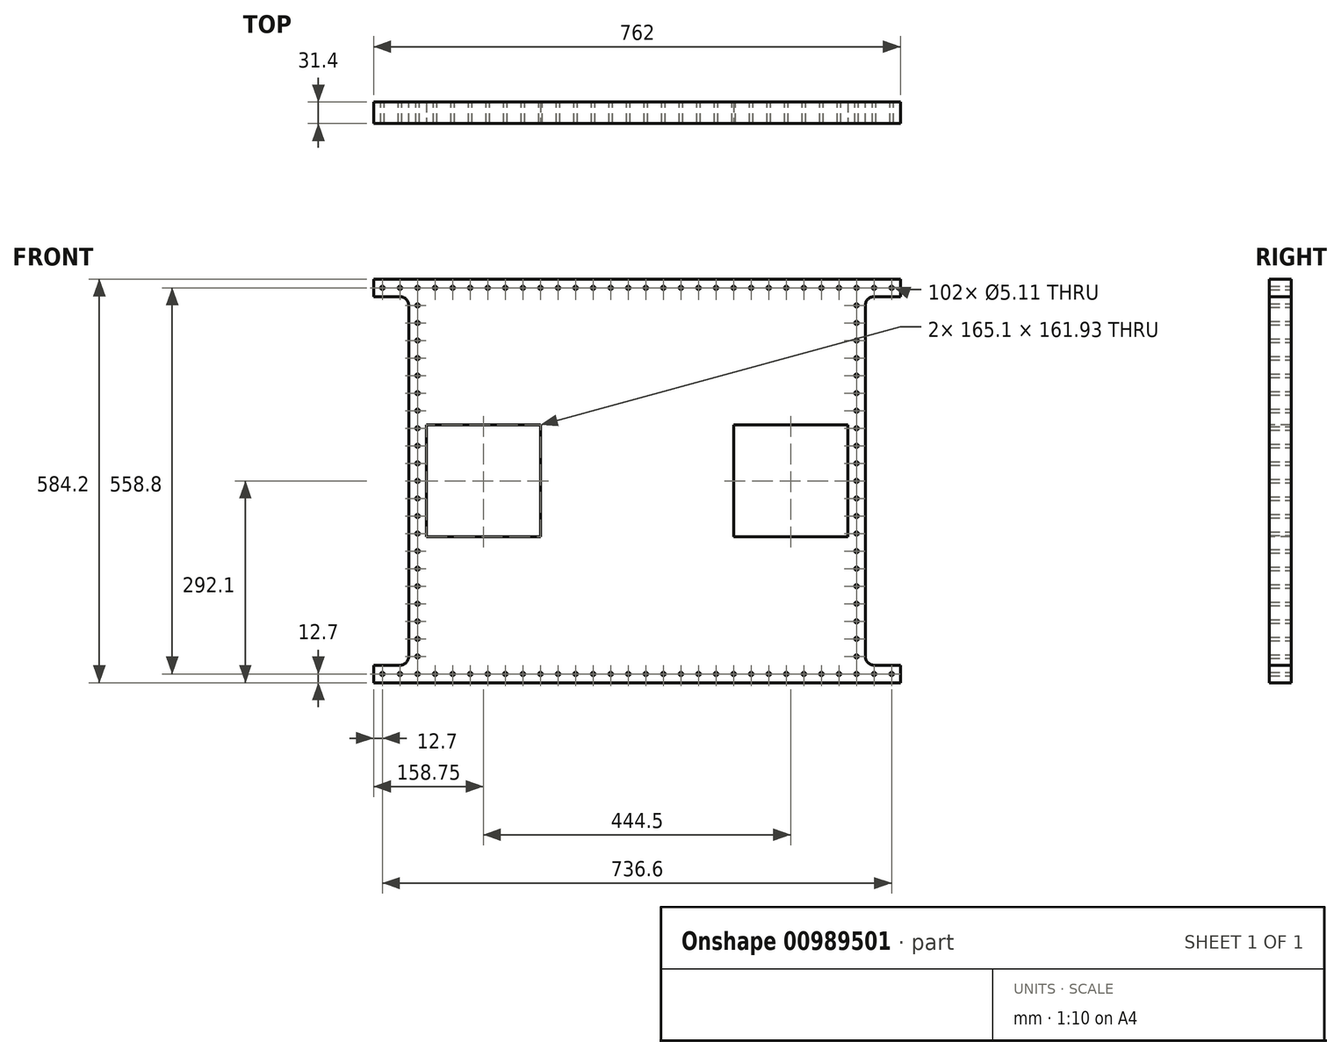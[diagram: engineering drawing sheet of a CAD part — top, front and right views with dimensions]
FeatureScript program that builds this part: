
annotation { "Feature Type Name" : "Feature", "Feature Type Description" : "" }
export const myFeature = defineFeature(function(context is Context, id is Id, definition is map)
    precondition{}
    {
        {
            var Q0;
            Q0=qCreatedBy(makeId("Front.planeOp"),FACE);
            var sketch = newSketch(context, id + "F0", { "sketchPlane" : qUnion([Q0])});
            skLineSegment(sketch, "E0", {"start": v(-381, 292.1) * mm, "end": v(381, 292.1) * mm});
            skLineSegment(sketch, "E1", {"start": v(381, 292.1) * mm, "end": v(381, 266.7) * mm});
            skLineSegment(sketch, "E2", {"start": v(381, 266.7) * mm, "end": v(342.9, 266.7) * mm});
            skLineSegment(sketch, "E3", {"start": v(330.2, 254) * mm, "end": v(330.2, -254) * mm});
            skLineSegment(sketch, "E4", {"start": v(342.9, -266.7) * mm, "end": v(381, -266.7) * mm});
            skLineSegment(sketch, "E5", {"start": v(381, -266.7) * mm, "end": v(381, -292.1) * mm});
            skLineSegment(sketch, "E6", {"start": v(381, -292.1) * mm, "end": v(-381, -292.1) * mm});
            skLineSegment(sketch, "E7", {"start": v(-381, -292.1) * mm, "end": v(-381, -266.7) * mm});
            skLineSegment(sketch, "E8", {"start": v(-381, -266.7) * mm, "end": v(-342.9, -266.7) * mm});
            skLineSegment(sketch, "E9", {"start": v(-330.2, -254) * mm, "end": v(-330.2, 254) * mm});
            skLineSegment(sketch, "E10", {"start": v(-342.9, 266.7) * mm, "end": v(-381, 266.7) * mm});
            skLineSegment(sketch, "E11", {"start": v(-381, 266.7) * mm, "end": v(-381, 292.1) * mm});
            skLineSegment(sketch, "E12", {"start": v(-381, 292.1) * mm, "end": v(0, 0) * mm, "construction": true});
            skLineSegment(sketch, "E13", {"start": v(0, 0) * mm, "end": v(381, -292.1) * mm, "construction": true});
            skLineSegment(sketch, "E14", {"start": v(-381, -292.1) * mm, "end": v(0, 0) * mm, "construction": true});
            skLineSegment(sketch, "E15", {"start": v(0, 0) * mm, "end": v(381, 292.1) * mm, "construction": true});
            skPoint(sketch, "E16.visualSharp", {"position": v(-330.2, 266.7) * mm});
            skArc(sketch, "E16.filletArc", {"start": v(-330.2, 254) * mm, "mid": v(-333.92, 262.98) * mm, "end": v(-342.9, 266.7) * mm});
            skPoint(sketch, "E17.visualSharp", {"position": v(-330.2, -266.7) * mm});
            skArc(sketch, "E17.filletArc", {"start": v(-342.9, -266.7) * mm, "mid": v(-333.92, -262.98) * mm, "end": v(-330.2, -254) * mm});
            skPoint(sketch, "E18.visualSharp", {"position": v(330.2, -266.7) * mm});
            skArc(sketch, "E18.filletArc", {"start": v(330.2, -254) * mm, "mid": v(333.92, -262.98) * mm, "end": v(342.9, -266.7) * mm});
            skPoint(sketch, "E19.visualSharp", {"position": v(330.2, 266.7) * mm});
            skArc(sketch, "E19.filletArc", {"start": v(342.9, 266.7) * mm, "mid": v(333.92, 262.98) * mm, "end": v(330.2, 254) * mm});
            skLineSegment(sketch, "E20", {"start": v(-330.2, 0) * mm, "end": v(330.2, 0) * mm, "construction": true});
            skLineSegment(sketch, "E21", {"start": v(0, 292.1) * mm, "end": v(0, -292.1) * mm, "construction": true});
            skCircle(sketch, "E22", {"center": v(-368.3, 279.4) * mm, "radius": 2.55 * mm});
            skCircle(sketch, "E23.1.0.0", {"center": v(-342.9, 279.4) * mm, "radius": 2.55 * mm});
            skCircle(sketch, "E23.2.0.0", {"center": v(-317.5, 279.4) * mm, "radius": 2.55 * mm});
            skCircle(sketch, "E23.3.0.0", {"center": v(-292.1, 279.4) * mm, "radius": 2.55 * mm});
            skCircle(sketch, "E23.4.0.0", {"center": v(-266.7, 279.4) * mm, "radius": 2.55 * mm});
            skCircle(sketch, "E23.5.0.0", {"center": v(-241.3, 279.4) * mm, "radius": 2.55 * mm});
            skCircle(sketch, "E23.6.0.0", {"center": v(-215.9, 279.4) * mm, "radius": 2.55 * mm});
            skCircle(sketch, "E23.7.0.0", {"center": v(-190.5, 279.4) * mm, "radius": 2.55 * mm});
            skCircle(sketch, "E23.8.0.0", {"center": v(-165.1, 279.4) * mm, "radius": 2.55 * mm});
            skCircle(sketch, "E23.9.0.0", {"center": v(-139.7, 279.4) * mm, "radius": 2.55 * mm});
            skCircle(sketch, "E23.10.0.0", {"center": v(-114.3, 279.4) * mm, "radius": 2.55 * mm});
            skCircle(sketch, "E23.11.0.0", {"center": v(-88.9, 279.4) * mm, "radius": 2.55 * mm});
            skCircle(sketch, "E23.12.0.0", {"center": v(-63.5, 279.4) * mm, "radius": 2.55 * mm});
            skCircle(sketch, "E23.13.0.0", {"center": v(-38.1, 279.4) * mm, "radius": 2.55 * mm});
            skCircle(sketch, "E23.14.0.0", {"center": v(-12.7, 279.4) * mm, "radius": 2.55 * mm});
            skCircle(sketch, "E23.15.0.0", {"center": v(12.7, 279.4) * mm, "radius": 2.55 * mm});
            skCircle(sketch, "E23.16.0.0", {"center": v(38.1, 279.4) * mm, "radius": 2.55 * mm});
            skCircle(sketch, "E23.17.0.0", {"center": v(63.5, 279.4) * mm, "radius": 2.55 * mm});
            skCircle(sketch, "E23.18.0.0", {"center": v(88.9, 279.4) * mm, "radius": 2.55 * mm});
            skCircle(sketch, "E23.19.0.0", {"center": v(114.3, 279.4) * mm, "radius": 2.55 * mm});
            skCircle(sketch, "E23.20.0.0", {"center": v(139.7, 279.4) * mm, "radius": 2.55 * mm});
            skCircle(sketch, "E23.21.0.0", {"center": v(165.1, 279.4) * mm, "radius": 2.55 * mm});
            skCircle(sketch, "E23.22.0.0", {"center": v(190.5, 279.4) * mm, "radius": 2.55 * mm});
            skCircle(sketch, "E23.23.0.0", {"center": v(215.9, 279.4) * mm, "radius": 2.55 * mm});
            skCircle(sketch, "E23.24.0.0", {"center": v(241.3, 279.4) * mm, "radius": 2.55 * mm});
            skCircle(sketch, "E23.25.0.0", {"center": v(266.7, 279.4) * mm, "radius": 2.55 * mm});
            skCircle(sketch, "E23.26.0.0", {"center": v(292.1, 279.4) * mm, "radius": 2.55 * mm});
            skCircle(sketch, "E23.27.0.0", {"center": v(317.5, 279.4) * mm, "radius": 2.55 * mm});
            skCircle(sketch, "E23.28.0.0", {"center": v(342.9, 279.4) * mm, "radius": 2.55 * mm});
            skCircle(sketch, "E23.29.0.0", {"center": v(368.3, 279.4) * mm, "radius": 2.55 * mm});
            skLineSegment(sketch, "E23.direction1", {"start": v(-368.3, 279.4) * mm, "end": v(-342.9, 279.4) * mm, "construction": true});
            skArc(sketch, "E24.MirrorCS", {"start": v(-330.2, -254) * mm, "mid": v(-333.92, -262.98) * mm, "end": v(-342.9, -266.7) * mm});
            skArc(sketch, "E25.MirrorCS", {"start": v(342.9, -266.7) * mm, "mid": v(333.92, -262.98) * mm, "end": v(330.2, -254) * mm});
            skCircle(sketch, "E26.MirrorC", {"center": v(-342.9, -279.4) * mm, "radius": 2.55 * mm});
            skCircle(sketch, "E27.MirrorC", {"center": v(-368.3, -279.4) * mm, "radius": 2.55 * mm});
            skCircle(sketch, "E28.MirrorC", {"center": v(-139.7, -279.4) * mm, "radius": 2.55 * mm});
            skCircle(sketch, "E29.MirrorC", {"center": v(266.7, -279.4) * mm, "radius": 2.55 * mm});
            skLineSegment(sketch, "E30.MirrorCS", {"start": v(-342.9, -266.7) * mm, "end": v(-381, -266.7) * mm});
            skCircle(sketch, "E31.MirrorC", {"center": v(-114.3, -279.4) * mm, "radius": 2.55 * mm});
            skCircle(sketch, "E32.MirrorC", {"center": v(292.1, -279.4) * mm, "radius": 2.55 * mm});
            skCircle(sketch, "E33.MirrorC", {"center": v(-88.9, -279.4) * mm, "radius": 2.55 * mm});
            skCircle(sketch, "E34.MirrorC", {"center": v(317.5, -279.4) * mm, "radius": 2.55 * mm});
            skCircle(sketch, "E35.MirrorC", {"center": v(-165.1, -279.4) * mm, "radius": 2.55 * mm});
            skCircle(sketch, "E36.MirrorC", {"center": v(-63.5, -279.4) * mm, "radius": 2.55 * mm});
            skCircle(sketch, "E37.MirrorC", {"center": v(342.9, -279.4) * mm, "radius": 2.55 * mm});
            skCircle(sketch, "E38.MirrorC", {"center": v(241.3, -279.4) * mm, "radius": 2.55 * mm});
            skCircle(sketch, "E39.MirrorC", {"center": v(-215.9, -279.4) * mm, "radius": 2.55 * mm});
            skCircle(sketch, "E40.MirrorC", {"center": v(-38.1, -279.4) * mm, "radius": 2.55 * mm});
            skCircle(sketch, "E41.MirrorC", {"center": v(190.5, -279.4) * mm, "radius": 2.55 * mm});
            skCircle(sketch, "E42.MirrorC", {"center": v(368.3, -279.4) * mm, "radius": 2.55 * mm});
            skCircle(sketch, "E43.MirrorC", {"center": v(165.1, -279.4) * mm, "radius": 2.55 * mm});
            skCircle(sketch, "E44.MirrorC", {"center": v(63.5, -279.4) * mm, "radius": 2.55 * mm});
            skCircle(sketch, "E45.MirrorC", {"center": v(-12.7, -279.4) * mm, "radius": 2.55 * mm});
            skCircle(sketch, "E46.MirrorC", {"center": v(114.3, -279.4) * mm, "radius": 2.55 * mm});
            skCircle(sketch, "E47.MirrorC", {"center": v(-266.7, -279.4) * mm, "radius": 2.55 * mm});
            skCircle(sketch, "E48.MirrorC", {"center": v(-292.1, -279.4) * mm, "radius": 2.55 * mm});
            skCircle(sketch, "E49.MirrorC", {"center": v(215.9, -279.4) * mm, "radius": 2.55 * mm});
            skCircle(sketch, "E50.MirrorC", {"center": v(139.7, -279.4) * mm, "radius": 2.55 * mm});
            skCircle(sketch, "E51.MirrorC", {"center": v(-241.3, -279.4) * mm, "radius": 2.55 * mm});
            skCircle(sketch, "E52.MirrorC", {"center": v(88.9, -279.4) * mm, "radius": 2.55 * mm});
            skCircle(sketch, "E53.MirrorC", {"center": v(38.1, -279.4) * mm, "radius": 2.55 * mm});
            skCircle(sketch, "E54.MirrorC", {"center": v(-190.5, -279.4) * mm, "radius": 2.55 * mm});
            skCircle(sketch, "E55.MirrorC", {"center": v(-317.5, -279.4) * mm, "radius": 2.55 * mm});
            skCircle(sketch, "E56.MirrorC", {"center": v(12.7, -279.4) * mm, "radius": 2.55 * mm});
            skLineSegment(sketch, "E57.MirrorCS", {"start": v(-381, -266.7) * mm, "end": v(-381, -292.1) * mm});
            skLineSegment(sketch, "E58.MirrorCS", {"start": v(381, -266.7) * mm, "end": v(342.9, -266.7) * mm});
            skLineSegment(sketch, "E59.MirrorCS", {"start": v(-368.3, -279.4) * mm, "end": v(-342.9, -279.4) * mm, "construction": true});
            skLineSegment(sketch, "E60.MirrorCS", {"start": v(-381, -292.1) * mm, "end": v(381, -292.1) * mm});
            skLineSegment(sketch, "E61.MirrorCS", {"start": v(381, -292.1) * mm, "end": v(381, -266.7) * mm});
            skCircle(sketch, "E62.0.1.0", {"center": v(-317.5, 254) * mm, "radius": 2.55 * mm});
            skCircle(sketch, "E62.0.2.0", {"center": v(-317.5, 228.6) * mm, "radius": 2.55 * mm});
            skCircle(sketch, "E62.0.3.0", {"center": v(-317.5, 203.2) * mm, "radius": 2.55 * mm});
            skCircle(sketch, "E62.0.4.0", {"center": v(-317.5, 177.8) * mm, "radius": 2.55 * mm});
            skCircle(sketch, "E62.0.5.0", {"center": v(-317.5, 152.4) * mm, "radius": 2.55 * mm});
            skCircle(sketch, "E62.0.6.0", {"center": v(-317.5, 127) * mm, "radius": 2.55 * mm});
            skCircle(sketch, "E62.0.7.0", {"center": v(-317.5, 101.6) * mm, "radius": 2.55 * mm});
            skCircle(sketch, "E62.0.8.0", {"center": v(-317.5, 76.2) * mm, "radius": 2.55 * mm});
            skCircle(sketch, "E62.0.9.0", {"center": v(-317.5, 50.8) * mm, "radius": 2.55 * mm});
            skCircle(sketch, "E62.0.10.0", {"center": v(-317.5, 25.4) * mm, "radius": 2.55 * mm});
            skCircle(sketch, "E62.0.11.0", {"center": v(-317.5, 0) * mm, "radius": 2.55 * mm});
            skCircle(sketch, "E62.0.12.0", {"center": v(-317.5, -25.4) * mm, "radius": 2.55 * mm});
            skCircle(sketch, "E62.0.13.0", {"center": v(-317.5, -50.8) * mm, "radius": 2.55 * mm});
            skCircle(sketch, "E62.0.14.0", {"center": v(-317.5, -76.2) * mm, "radius": 2.55 * mm});
            skCircle(sketch, "E62.0.15.0", {"center": v(-317.5, -101.6) * mm, "radius": 2.55 * mm});
            skCircle(sketch, "E62.0.16.0", {"center": v(-317.5, -127) * mm, "radius": 2.55 * mm});
            skCircle(sketch, "E62.0.17.0", {"center": v(-317.5, -152.4) * mm, "radius": 2.55 * mm});
            skCircle(sketch, "E62.0.18.0", {"center": v(-317.5, -177.8) * mm, "radius": 2.55 * mm});
            skCircle(sketch, "E62.0.19.0", {"center": v(-317.5, -203.2) * mm, "radius": 2.55 * mm});
            skCircle(sketch, "E62.0.20.0", {"center": v(-317.5, -228.6) * mm, "radius": 2.55 * mm});
            skCircle(sketch, "E62.0.21.0", {"center": v(-317.5, -254) * mm, "radius": 2.55 * mm});
            skLineSegment(sketch, "E62.direction1", {"start": v(-317.5, 279.4) * mm, "end": v(-317.5, 279.4) * mm});
            skLineSegment(sketch, "E62.direction2", {"start": v(-317.5, 279.4) * mm, "end": v(-317.5, 254) * mm, "construction": true});
            skCircle(sketch, "E63.MirrorC", {"center": v(317.5, 254) * mm, "radius": 2.55 * mm});
            skArc(sketch, "E64.MirrorCS", {"start": v(330.2, 254) * mm, "mid": v(333.92, 262.98) * mm, "end": v(342.9, 266.7) * mm});
            skCircle(sketch, "E65.MirrorC", {"center": v(317.5, -152.4) * mm, "radius": 2.55 * mm});
            skCircle(sketch, "E66.MirrorC", {"center": v(317.5, 152.4) * mm, "radius": 2.55 * mm});
            skCircle(sketch, "E67.MirrorC", {"center": v(317.5, -254) * mm, "radius": 2.55 * mm});
            skCircle(sketch, "E68.MirrorC", {"center": v(317.5, -76.2) * mm, "radius": 2.55 * mm});
            skCircle(sketch, "E69.MirrorC", {"center": v(317.5, 76.2) * mm, "radius": 2.55 * mm});
            skCircle(sketch, "E70.MirrorC", {"center": v(317.5, -25.4) * mm, "radius": 2.55 * mm});
            skCircle(sketch, "E71.MirrorC", {"center": v(317.5, 203.2) * mm, "radius": 2.55 * mm});
            skCircle(sketch, "E72.MirrorC", {"center": v(317.5, 101.6) * mm, "radius": 2.55 * mm});
            skCircle(sketch, "E73.MirrorC", {"center": v(317.5, -177.8) * mm, "radius": 2.55 * mm});
            skCircle(sketch, "E74.MirrorC", {"center": v(317.5, 228.6) * mm, "radius": 2.55 * mm});
            skCircle(sketch, "E75.MirrorC", {"center": v(317.5, -228.6) * mm, "radius": 2.55 * mm});
            skCircle(sketch, "E76.MirrorC", {"center": v(317.5, 0) * mm, "radius": 2.55 * mm});
            skCircle(sketch, "E77.MirrorC", {"center": v(317.5, 127) * mm, "radius": 2.55 * mm});
            skCircle(sketch, "E78.MirrorC", {"center": v(317.5, -50.8) * mm, "radius": 2.55 * mm});
            skCircle(sketch, "E79.MirrorC", {"center": v(317.5, 50.8) * mm, "radius": 2.55 * mm});
            skCircle(sketch, "E80.MirrorC", {"center": v(317.5, -203.2) * mm, "radius": 2.55 * mm});
            skCircle(sketch, "E81.MirrorC", {"center": v(317.5, 177.8) * mm, "radius": 2.55 * mm});
            skCircle(sketch, "E82.MirrorC", {"center": v(317.5, -101.6) * mm, "radius": 2.55 * mm});
            skCircle(sketch, "E83.MirrorC", {"center": v(317.5, 25.4) * mm, "radius": 2.55 * mm});
            skCircle(sketch, "E84.MirrorC", {"center": v(317.5, -127) * mm, "radius": 2.55 * mm});
            skLineSegment(sketch, "E85.MirrorCS", {"start": v(342.9, 266.7) * mm, "end": v(381, 266.7) * mm});
            skLineSegment(sketch, "E86.MirrorCS", {"start": v(330.2, -254) * mm, "end": v(330.2, 254) * mm});
            skSolve(sketch);
        }
        {
            var Q0;
            Q0 = qSketchRegion(id + "F0", true);
            extrude(context, id + "F1", {"entities" : qUnion([Q0]), "depth" : 6 * mm, "offsetDistance" : 25.4 * mm});
        }
        {
            var Q0;
            Q0=makeQuery(id+"F1.opExtrude","CAP_FACE",FACE,{"disambiguationData":[OSD([sQuery(id+"F0.wireOp",EDGE,"E0"),sQuery(id+"F0.wireOp",EDGE,"E1"),sQuery(id+"F0.wireOp",EDGE,"E9"),sQuery(id+"F0.wireOp",EDGE,"E10"),sQuery(id+"F0.wireOp",EDGE,"E11"),sQuery(id+"F0.wireOp",EDGE,"E16.filletArc"),sQuery(id+"F0.wireOp",EDGE,"E22"),sQuery(id+"F0.wireOp",EDGE,"E23.1.0.0"),sQuery(id+"F0.wireOp",EDGE,"E23.2.0.0"),sQuery(id+"F0.wireOp",EDGE,"E23.3.0.0"),sQuery(id+"F0.wireOp",EDGE,"E23.4.0.0"),sQuery(id+"F0.wireOp",EDGE,"E23.5.0.0"),sQuery(id+"F0.wireOp",EDGE,"E23.6.0.0"),sQuery(id+"F0.wireOp",EDGE,"E23.7.0.0"),sQuery(id+"F0.wireOp",EDGE,"E23.8.0.0"),sQuery(id+"F0.wireOp",EDGE,"E23.9.0.0"),sQuery(id+"F0.wireOp",EDGE,"E23.10.0.0"),sQuery(id+"F0.wireOp",EDGE,"E23.11.0.0"),sQuery(id+"F0.wireOp",EDGE,"E23.12.0.0"),sQuery(id+"F0.wireOp",EDGE,"E23.13.0.0"),sQuery(id+"F0.wireOp",EDGE,"E23.14.0.0"),sQuery(id+"F0.wireOp",EDGE,"E23.15.0.0"),sQuery(id+"F0.wireOp",EDGE,"E23.16.0.0"),sQuery(id+"F0.wireOp",EDGE,"E23.17.0.0"),sQuery(id+"F0.wireOp",EDGE,"E23.18.0.0"),sQuery(id+"F0.wireOp",EDGE,"E23.19.0.0"),sQuery(id+"F0.wireOp",EDGE,"E23.20.0.0"),sQuery(id+"F0.wireOp",EDGE,"E23.21.0.0"),sQuery(id+"F0.wireOp",EDGE,"E23.22.0.0"),sQuery(id+"F0.wireOp",EDGE,"E23.23.0.0"),sQuery(id+"F0.wireOp",EDGE,"E23.24.0.0"),sQuery(id+"F0.wireOp",EDGE,"E23.25.0.0"),sQuery(id+"F0.wireOp",EDGE,"E23.26.0.0"),sQuery(id+"F0.wireOp",EDGE,"E23.27.0.0"),sQuery(id+"F0.wireOp",EDGE,"E23.28.0.0"),sQuery(id+"F0.wireOp",EDGE,"E23.29.0.0"),sQuery(id+"F0.wireOp",EDGE,"E23.30.0.0"),sQuery(id+"F0.wireOp",EDGE,"E23.31.0.0"),sQuery(id+"F0.wireOp",EDGE,"E24.MirrorCS"),sQuery(id+"F0.wireOp",EDGE,"E25.MirrorCS"),sQuery(id+"F0.wireOp",EDGE,"E26.MirrorC"),sQuery(id+"F0.wireOp",EDGE,"E27.MirrorC"),sQuery(id+"F0.wireOp",EDGE,"E28.MirrorC"),sQuery(id+"F0.wireOp",EDGE,"E29.MirrorC"),sQuery(id+"F0.wireOp",EDGE,"E30.MirrorCS"),sQuery(id+"F0.wireOp",EDGE,"E31.MirrorC"),sQuery(id+"F0.wireOp",EDGE,"E32.MirrorC"),sQuery(id+"F0.wireOp",EDGE,"E33.MirrorC"),sQuery(id+"F0.wireOp",EDGE,"E34.MirrorC"),sQuery(id+"F0.wireOp",EDGE,"E35.MirrorC"),sQuery(id+"F0.wireOp",EDGE,"E36.MirrorC"),sQuery(id+"F0.wireOp",EDGE,"E37.MirrorC"),sQuery(id+"F0.wireOp",EDGE,"E38.MirrorC"),sQuery(id+"F0.wireOp",EDGE,"E39.MirrorC"),sQuery(id+"F0.wireOp",EDGE,"E40.MirrorC"),sQuery(id+"F0.wireOp",EDGE,"E41.MirrorC"),sQuery(id+"F0.wireOp",EDGE,"E42.MirrorC"),sQuery(id+"F0.wireOp",EDGE,"E43.MirrorC"),sQuery(id+"F0.wireOp",EDGE,"E44.MirrorC"),sQuery(id+"F0.wireOp",EDGE,"E45.MirrorC"),sQuery(id+"F0.wireOp",EDGE,"E46.MirrorC"),sQuery(id+"F0.wireOp",EDGE,"E47.MirrorC"),sQuery(id+"F0.wireOp",EDGE,"E48.MirrorC"),sQuery(id+"F0.wireOp",EDGE,"E49.MirrorC"),sQuery(id+"F0.wireOp",EDGE,"E50.MirrorC"),sQuery(id+"F0.wireOp",EDGE,"E51.MirrorC"),sQuery(id+"F0.wireOp",EDGE,"E268.MirrorC"),sQuery(id+"F0.wireOp",EDGE,"E52.MirrorC"),sQuery(id+"F0.wireOp",EDGE,"E270.MirrorC"),sQuery(id+"F0.wireOp",EDGE,"E53.MirrorC"),sQuery(id+"F0.wireOp",EDGE,"E54.MirrorC"),sQuery(id+"F0.wireOp",EDGE,"E56.MirrorC"),sQuery(id+"F0.wireOp",EDGE,"E57.MirrorCS"),sQuery(id+"F0.wireOp",EDGE,"E60.MirrorCS"),sQuery(id+"F0.wireOp",EDGE,"E61.MirrorCS"),sQuery(id+"F0.wireOp",EDGE,"E62.0.1.0"),sQuery(id+"F0.wireOp",EDGE,"E62.0.2.0"),sQuery(id+"F0.wireOp",EDGE,"E62.0.3.0"),sQuery(id+"F0.wireOp",EDGE,"E62.0.4.0"),sQuery(id+"F0.wireOp",EDGE,"E62.0.5.0"),sQuery(id+"F0.wireOp",EDGE,"E62.0.6.0"),sQuery(id+"F0.wireOp",EDGE,"E62.0.7.0"),sQuery(id+"F0.wireOp",EDGE,"E62.0.8.0"),sQuery(id+"F0.wireOp",EDGE,"E62.0.9.0"),sQuery(id+"F0.wireOp",EDGE,"E62.0.10.0"),sQuery(id+"F0.wireOp",EDGE,"E62.0.11.0"),sQuery(id+"F0.wireOp",EDGE,"E62.0.12.0"),sQuery(id+"F0.wireOp",EDGE,"E62.0.13.0"),sQuery(id+"F0.wireOp",EDGE,"E62.0.14.0"),sQuery(id+"F0.wireOp",EDGE,"E62.0.15.0"),sQuery(id+"F0.wireOp",EDGE,"E62.0.16.0"),sQuery(id+"F0.wireOp",EDGE,"E62.0.17.0"),sQuery(id+"F0.wireOp",EDGE,"E62.0.18.0"),sQuery(id+"F0.wireOp",EDGE,"E62.0.19.0"),sQuery(id+"F0.wireOp",EDGE,"E62.0.20.0"),sQuery(id+"F0.wireOp",EDGE,"E62.0.21.0"),sQuery(id+"F0.wireOp",EDGE,"E55.MirrorC"),sQuery(id+"F0.wireOp",EDGE,"E63.MirrorC"),sQuery(id+"F0.wireOp",EDGE,"E64.MirrorCS"),sQuery(id+"F0.wireOp",EDGE,"E65.MirrorC"),sQuery(id+"F0.wireOp",EDGE,"E66.MirrorC"),sQuery(id+"F0.wireOp",EDGE,"E67.MirrorC"),sQuery(id+"F0.wireOp",EDGE,"E68.MirrorC"),sQuery(id+"F0.wireOp",EDGE,"E69.MirrorC"),sQuery(id+"F0.wireOp",EDGE,"E70.MirrorC"),sQuery(id+"F0.wireOp",EDGE,"E71.MirrorC"),sQuery(id+"F0.wireOp",EDGE,"E72.MirrorC"),sQuery(id+"F0.wireOp",EDGE,"E73.MirrorC"),sQuery(id+"F0.wireOp",EDGE,"E74.MirrorC"),sQuery(id+"F0.wireOp",EDGE,"E75.MirrorC"),sQuery(id+"F0.wireOp",EDGE,"E76.MirrorC"),sQuery(id+"F0.wireOp",EDGE,"E77.MirrorC"),sQuery(id+"F0.wireOp",EDGE,"E78.MirrorC"),sQuery(id+"F0.wireOp",EDGE,"E79.MirrorC"),sQuery(id+"F0.wireOp",EDGE,"E80.MirrorC"),sQuery(id+"F0.wireOp",EDGE,"E81.MirrorC"),sQuery(id+"F0.wireOp",EDGE,"E82.MirrorC"),sQuery(id+"F0.wireOp",EDGE,"E83.MirrorC"),sQuery(id+"F0.wireOp",EDGE,"E84.MirrorC"),sQuery(id+"F0.wireOp",EDGE,"E85.MirrorCS"),sQuery(id+"F0.wireOp",EDGE,"E86.MirrorCS"),sQuery(id+"F0.wireOp",EDGE,"E58.MirrorCS")])],"isStart":false});
            var sketch = newSketch(context, id + "F2", { "sketchPlane" : qUnion([Q0])});
            skLineSegment(sketch, "E87.bottom", {"start": v(-304.8, 80.96) * mm, "end": v(-139.7, 80.96) * mm});
            skLineSegment(sketch, "E87.top", {"start": v(-304.8, -80.96) * mm, "end": v(-139.7, -80.96) * mm});
            skLineSegment(sketch, "E87.left", {"start": v(-304.8, 80.96) * mm, "end": v(-304.8, -80.96) * mm});
            skLineSegment(sketch, "E87.right", {"start": v(-139.7, 80.96) * mm, "end": v(-139.7, -80.96) * mm});
            skPoint(sketch, "E87.middle", {"position": v(-222.25, 0) * mm});
            skLineSegment(sketch, "E88.bottom", {"start": v(304.8, 80.96) * mm, "end": v(139.7, 80.96) * mm});
            skLineSegment(sketch, "E88.top", {"start": v(304.8, -80.96) * mm, "end": v(139.7, -80.96) * mm});
            skLineSegment(sketch, "E88.left", {"start": v(304.8, 80.96) * mm, "end": v(304.8, -80.96) * mm});
            skLineSegment(sketch, "E88.right", {"start": v(139.7, 80.96) * mm, "end": v(139.7, -80.96) * mm});
            skPoint(sketch, "E88.middle", {"position": v(222.25, 0) * mm});
            skLineSegment(sketch, "E89", {"start": v(304.8, 292.1) * mm, "end": v(304.8, -292.1) * mm, "construction": true});
            skLineSegment(sketch, "E90", {"start": v(-304.8, -292.1) * mm, "end": v(-304.8, 292.1) * mm, "construction": true});
            skSolve(sketch);
        }
        {
            var Q0;
            Q0 = qSketchRegion(id + "F2", true);
            extrude(context, id + "F3", {"entities" : qUnion([Q0]), "operationType" : NewBodyOperationType.REMOVE, "oppositeDirection" : true, "depth" : 25.4 * mm, "offsetDistance" : 25.4 * mm});
        }
        {
            var Q0;
            Q0=makeQuery(id+"F1.opExtrude","CAP_FACE",FACE,{"disambiguationData":[OSD([sQuery(id+"F0.wireOp",EDGE,"E0"),sQuery(id+"F0.wireOp",EDGE,"E1"),sQuery(id+"F0.wireOp",EDGE,"E9"),sQuery(id+"F0.wireOp",EDGE,"E10"),sQuery(id+"F0.wireOp",EDGE,"E11"),sQuery(id+"F0.wireOp",EDGE,"E16.filletArc"),sQuery(id+"F0.wireOp",EDGE,"E22"),sQuery(id+"F0.wireOp",EDGE,"E23.1.0.0"),sQuery(id+"F0.wireOp",EDGE,"E23.2.0.0"),sQuery(id+"F0.wireOp",EDGE,"E23.3.0.0"),sQuery(id+"F0.wireOp",EDGE,"E23.4.0.0"),sQuery(id+"F0.wireOp",EDGE,"E23.5.0.0"),sQuery(id+"F0.wireOp",EDGE,"E23.6.0.0"),sQuery(id+"F0.wireOp",EDGE,"E23.7.0.0"),sQuery(id+"F0.wireOp",EDGE,"E23.8.0.0"),sQuery(id+"F0.wireOp",EDGE,"E23.9.0.0"),sQuery(id+"F0.wireOp",EDGE,"E23.10.0.0"),sQuery(id+"F0.wireOp",EDGE,"E23.11.0.0"),sQuery(id+"F0.wireOp",EDGE,"E23.12.0.0"),sQuery(id+"F0.wireOp",EDGE,"E23.13.0.0"),sQuery(id+"F0.wireOp",EDGE,"E23.14.0.0"),sQuery(id+"F0.wireOp",EDGE,"E23.15.0.0"),sQuery(id+"F0.wireOp",EDGE,"E23.16.0.0"),sQuery(id+"F0.wireOp",EDGE,"E23.17.0.0"),sQuery(id+"F0.wireOp",EDGE,"E23.18.0.0"),sQuery(id+"F0.wireOp",EDGE,"E23.19.0.0"),sQuery(id+"F0.wireOp",EDGE,"E23.20.0.0"),sQuery(id+"F0.wireOp",EDGE,"E23.21.0.0"),sQuery(id+"F0.wireOp",EDGE,"E23.22.0.0"),sQuery(id+"F0.wireOp",EDGE,"E23.23.0.0"),sQuery(id+"F0.wireOp",EDGE,"E23.24.0.0"),sQuery(id+"F0.wireOp",EDGE,"E23.25.0.0"),sQuery(id+"F0.wireOp",EDGE,"E23.26.0.0"),sQuery(id+"F0.wireOp",EDGE,"E23.27.0.0"),sQuery(id+"F0.wireOp",EDGE,"E23.28.0.0"),sQuery(id+"F0.wireOp",EDGE,"E23.29.0.0"),sQuery(id+"F0.wireOp",EDGE,"E24.MirrorCS"),sQuery(id+"F0.wireOp",EDGE,"E25.MirrorCS"),sQuery(id+"F0.wireOp",EDGE,"E26.MirrorC"),sQuery(id+"F0.wireOp",EDGE,"E27.MirrorC"),sQuery(id+"F0.wireOp",EDGE,"E28.MirrorC"),sQuery(id+"F0.wireOp",EDGE,"E29.MirrorC"),sQuery(id+"F0.wireOp",EDGE,"E30.MirrorCS"),sQuery(id+"F0.wireOp",EDGE,"E31.MirrorC"),sQuery(id+"F0.wireOp",EDGE,"E32.MirrorC"),sQuery(id+"F0.wireOp",EDGE,"E33.MirrorC"),sQuery(id+"F0.wireOp",EDGE,"E34.MirrorC"),sQuery(id+"F0.wireOp",EDGE,"E35.MirrorC"),sQuery(id+"F0.wireOp",EDGE,"E36.MirrorC"),sQuery(id+"F0.wireOp",EDGE,"E37.MirrorC"),sQuery(id+"F0.wireOp",EDGE,"E38.MirrorC"),sQuery(id+"F0.wireOp",EDGE,"E39.MirrorC"),sQuery(id+"F0.wireOp",EDGE,"E40.MirrorC"),sQuery(id+"F0.wireOp",EDGE,"E41.MirrorC"),sQuery(id+"F0.wireOp",EDGE,"E42.MirrorC"),sQuery(id+"F0.wireOp",EDGE,"E43.MirrorC"),sQuery(id+"F0.wireOp",EDGE,"E44.MirrorC"),sQuery(id+"F0.wireOp",EDGE,"E45.MirrorC"),sQuery(id+"F0.wireOp",EDGE,"E46.MirrorC"),sQuery(id+"F0.wireOp",EDGE,"E47.MirrorC"),sQuery(id+"F0.wireOp",EDGE,"E48.MirrorC"),sQuery(id+"F0.wireOp",EDGE,"E49.MirrorC"),sQuery(id+"F0.wireOp",EDGE,"E50.MirrorC"),sQuery(id+"F0.wireOp",EDGE,"E51.MirrorC"),sQuery(id+"F0.wireOp",EDGE,"E52.MirrorC"),sQuery(id+"F0.wireOp",EDGE,"E53.MirrorC"),sQuery(id+"F0.wireOp",EDGE,"E54.MirrorC"),sQuery(id+"F0.wireOp",EDGE,"E56.MirrorC"),sQuery(id+"F0.wireOp",EDGE,"E57.MirrorCS"),sQuery(id+"F0.wireOp",EDGE,"E60.MirrorCS"),sQuery(id+"F0.wireOp",EDGE,"E61.MirrorCS"),sQuery(id+"F0.wireOp",EDGE,"E62.0.1.0"),sQuery(id+"F0.wireOp",EDGE,"E62.0.2.0"),sQuery(id+"F0.wireOp",EDGE,"E62.0.3.0"),sQuery(id+"F0.wireOp",EDGE,"E62.0.4.0"),sQuery(id+"F0.wireOp",EDGE,"E62.0.5.0"),sQuery(id+"F0.wireOp",EDGE,"E62.0.6.0"),sQuery(id+"F0.wireOp",EDGE,"E62.0.7.0"),sQuery(id+"F0.wireOp",EDGE,"E62.0.8.0"),sQuery(id+"F0.wireOp",EDGE,"E62.0.9.0"),sQuery(id+"F0.wireOp",EDGE,"E62.0.10.0"),sQuery(id+"F0.wireOp",EDGE,"E62.0.11.0"),sQuery(id+"F0.wireOp",EDGE,"E62.0.12.0"),sQuery(id+"F0.wireOp",EDGE,"E62.0.13.0"),sQuery(id+"F0.wireOp",EDGE,"E62.0.14.0"),sQuery(id+"F0.wireOp",EDGE,"E62.0.15.0"),sQuery(id+"F0.wireOp",EDGE,"E62.0.16.0"),sQuery(id+"F0.wireOp",EDGE,"E62.0.17.0"),sQuery(id+"F0.wireOp",EDGE,"E62.0.18.0"),sQuery(id+"F0.wireOp",EDGE,"E62.0.19.0"),sQuery(id+"F0.wireOp",EDGE,"E62.0.20.0"),sQuery(id+"F0.wireOp",EDGE,"E62.0.21.0"),sQuery(id+"F0.wireOp",EDGE,"E55.MirrorC"),sQuery(id+"F0.wireOp",EDGE,"E63.MirrorC"),sQuery(id+"F0.wireOp",EDGE,"E64.MirrorCS"),sQuery(id+"F0.wireOp",EDGE,"E65.MirrorC"),sQuery(id+"F0.wireOp",EDGE,"E66.MirrorC"),sQuery(id+"F0.wireOp",EDGE,"E67.MirrorC"),sQuery(id+"F0.wireOp",EDGE,"E68.MirrorC"),sQuery(id+"F0.wireOp",EDGE,"E69.MirrorC"),sQuery(id+"F0.wireOp",EDGE,"E70.MirrorC"),sQuery(id+"F0.wireOp",EDGE,"E71.MirrorC"),sQuery(id+"F0.wireOp",EDGE,"E72.MirrorC"),sQuery(id+"F0.wireOp",EDGE,"E73.MirrorC"),sQuery(id+"F0.wireOp",EDGE,"E74.MirrorC"),sQuery(id+"F0.wireOp",EDGE,"E75.MirrorC"),sQuery(id+"F0.wireOp",EDGE,"E76.MirrorC"),sQuery(id+"F0.wireOp",EDGE,"E77.MirrorC"),sQuery(id+"F0.wireOp",EDGE,"E78.MirrorC"),sQuery(id+"F0.wireOp",EDGE,"E79.MirrorC"),sQuery(id+"F0.wireOp",EDGE,"E80.MirrorC"),sQuery(id+"F0.wireOp",EDGE,"E81.MirrorC"),sQuery(id+"F0.wireOp",EDGE,"E82.MirrorC"),sQuery(id+"F0.wireOp",EDGE,"E83.MirrorC"),sQuery(id+"F0.wireOp",EDGE,"E84.MirrorC"),sQuery(id+"F0.wireOp",EDGE,"E85.MirrorCS"),sQuery(id+"F0.wireOp",EDGE,"E86.MirrorCS"),sQuery(id+"F0.wireOp",EDGE,"E58.MirrorCS")])],"isStart":false});
            extrude(context, id + "F4", {"entities" : qUnion([Q0]), "operationType" : NewBodyOperationType.ADD, "depth" : 25.4 * mm, "offsetDistance" : 25.4 * mm});
        }
    });
